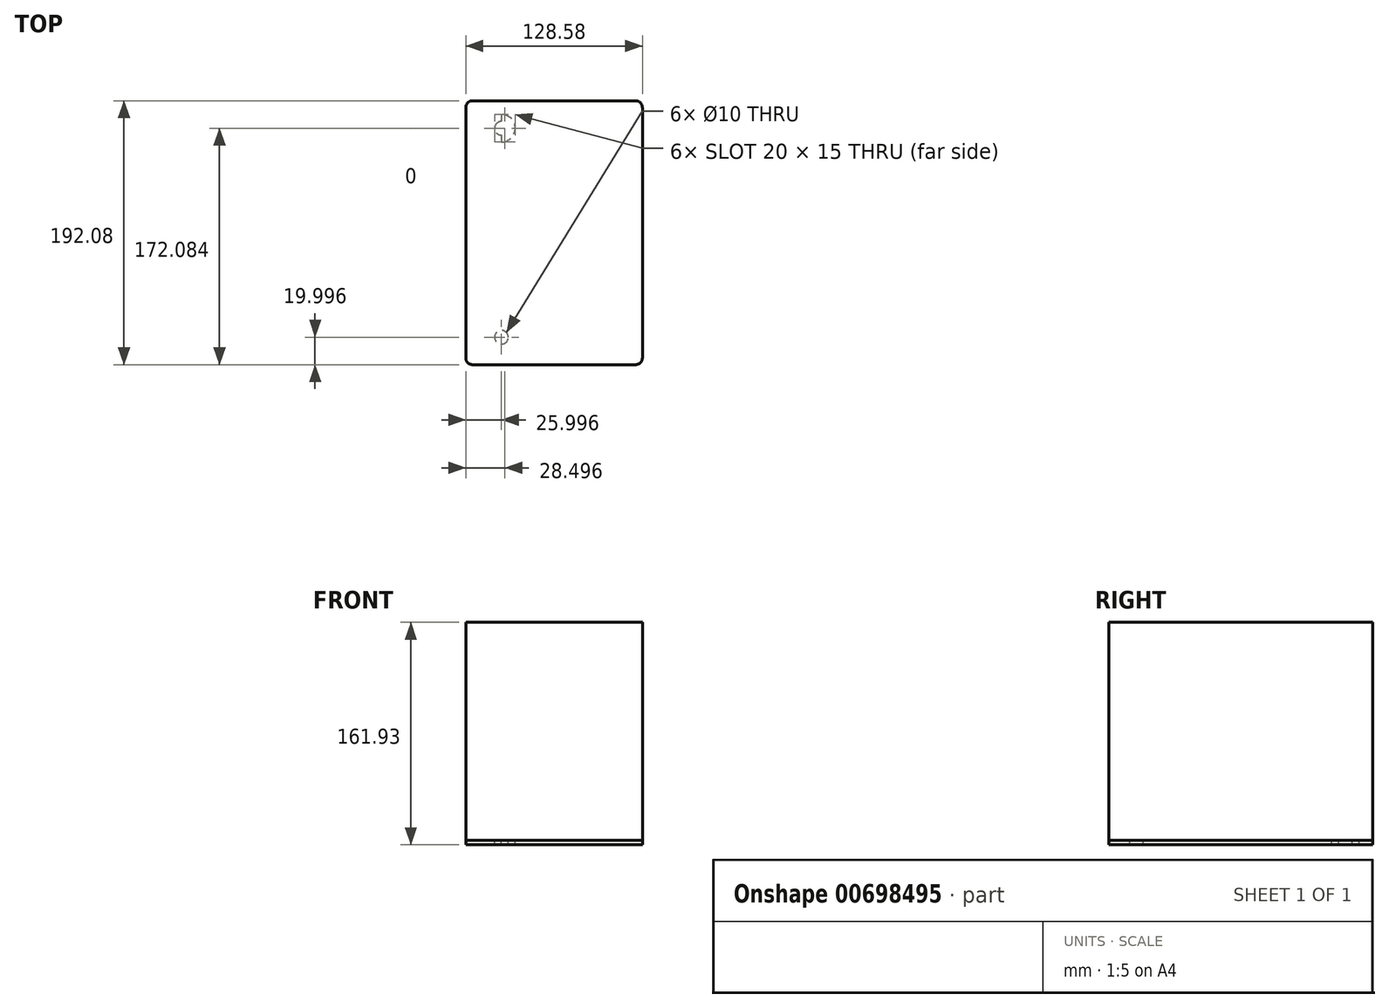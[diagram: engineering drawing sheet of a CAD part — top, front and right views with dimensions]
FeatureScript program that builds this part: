
annotation { "Feature Type Name" : "Feature", "Feature Type Description" : "" }
export const myFeature = defineFeature(function(context is Context, id is Id, definition is map)
    precondition{}
    {
        {
            var Q0;
            Q0=qCreatedBy(makeId("Top.planeOp"),FACE);
            var sketch = newSketch(context, id + "F0", { "sketchPlane" : qUnion([Q0])});
            skLineSegment(sketch, "E0.bottom", {"start": v(-59.3, -96.04) * mm, "end": v(59.3, -96.04) * mm});
            skLineSegment(sketch, "E0.top", {"start": v(-59.3, 96.04) * mm, "end": v(59.3, 96.04) * mm});
            skLineSegment(sketch, "E0.left", {"start": v(-64.3, -91.04) * mm, "end": v(-64.3, 91.04) * mm});
            skLineSegment(sketch, "E0.right", {"start": v(64.3, -91.04) * mm, "end": v(64.3, 91.04) * mm});
            skPoint(sketch, "E1.visualSharp", {"position": v(-64.3, -96.04) * mm});
            skArc(sketch, "E1.filletArc", {"start": v(-64.3, -91.04) * mm, "mid": v(-62.83, -94.58) * mm, "end": v(-59.3, -96.04) * mm});
            skPoint(sketch, "E2.visualSharp", {"position": v(-64.3, 96.04) * mm});
            skArc(sketch, "E2.filletArc", {"start": v(-59.3, 96.04) * mm, "mid": v(-62.83, 94.58) * mm, "end": v(-64.3, 91.04) * mm});
            skPoint(sketch, "E3.visualSharp", {"position": v(64.3, 96.04) * mm});
            skArc(sketch, "E3.filletArc", {"start": v(64.3, 91.04) * mm, "mid": v(62.83, 94.58) * mm, "end": v(59.3, 96.04) * mm});
            skPoint(sketch, "E4.visualSharp", {"position": v(64.3, -96.04) * mm});
            skArc(sketch, "E4.filletArc", {"start": v(59.3, -96.04) * mm, "mid": v(62.83, -94.58) * mm, "end": v(64.3, -91.04) * mm});
            skSolve(sketch);
        }
        {
            var Q0;
            Q0 = qSketchRegion(id + "F0", true);
            extrude(context, id + "F1", {"entities" : qUnion([Q0]), "depth" : 158.75 * mm, "offsetDistance" : 25 * mm});
        }
        {
            var Q0;
            Q0=makeQuery(id+"F1.opExtrude","CAP_FACE",FACE,{"disambiguationData":[OSD([sQuery(id+"F0.wireOp",EDGE,"E0.bottom"),sQuery(id+"F0.wireOp",EDGE,"E0.top"),sQuery(id+"F0.wireOp",EDGE,"E0.left"),sQuery(id+"F0.wireOp",EDGE,"E0.right"),sQuery(id+"F0.wireOp",EDGE,"E1.filletArc"),sQuery(id+"F0.wireOp",EDGE,"E2.filletArc"),sQuery(id+"F0.wireOp",EDGE,"E3.filletArc"),sQuery(id+"F0.wireOp",EDGE,"E4.filletArc")])],"isStart":true});
            var sketch = newSketch(context, id + "F2", { "sketchPlane" : qUnion([Q0])});
            skLineSegment(sketch, "E5.bottom", {"start": v(-38.3, 86.04) * mm, "end": v(-58.3, 86.04) * mm});
            skLineSegment(sketch, "E5.top", {"start": v(-38.3, 66.04) * mm, "end": v(-58.3, 66.04) * mm});
            skLineSegment(sketch, "E5.left", {"start": v(-38.3, 86.04) * mm, "end": v(-38.3, 66.04) * mm});
            skLineSegment(sketch, "E5.right", {"start": v(-58.3, 86.04) * mm, "end": v(-58.3, 66.04) * mm});
            skArc(sketch, "E6", {"start": v(-38.3, 66.04) * mm, "mid": v(-28.3, 76.04) * mm, "end": v(-38.3, 86.04) * mm});
            skCircle(sketch, "E7", {"center": v(-38.3, 76.04) * mm, "radius": 5 * mm});
            skLineSegment(sketch, "E8", {"start": v(-53.01, 0) * mm, "end": v(36.14, 0) * mm, "construction": true});
            skLineSegment(sketch, "E9.MirrorCS", {"start": v(-38.3, -86.04) * mm, "end": v(-58.3, -86.04) * mm});
            skCircle(sketch, "E10.MirrorC", {"center": v(-38.3, -76.04) * mm, "radius": 5 * mm});
            skLineSegment(sketch, "E11.MirrorCS", {"start": v(-38.3, -86.04) * mm, "end": v(-38.3, -66.04) * mm});
            skLineSegment(sketch, "E12.MirrorCS", {"start": v(-38.3, -66.04) * mm, "end": v(-58.3, -66.04) * mm});
            skArc(sketch, "E13.MirrorCS", {"start": v(-38.3, -66.04) * mm, "mid": v(-28.3, -76.04) * mm, "end": v(-38.3, -86.04) * mm});
            skLineSegment(sketch, "E14.MirrorCS", {"start": v(-58.3, -86.04) * mm, "end": v(-58.3, -66.04) * mm});
            skSolve(sketch);
        }
        {
            var Q0;
            {var subQ5=sQuery(id+"F2.wireOp",EDGE,"E5.bottom");Q0=makeQuery(id+"F2.imprint","IMPRINT",FACE,{"disambiguationData":[TD([[makeQuery(id+"F2.imprint","IMPRINT",EDGE,{"derivedFrom":subQ5}),1.0]])]});}
            var Q1;
            {var subQ0=sQuery(id+"F2.wireOp",EDGE,"E6");Q1=makeQuery(id+"F2.imprint","IMPRINT",FACE,{"disambiguationData":[TD([[makeQuery(id+"F2.imprint","IMPRINT",EDGE,{"derivedFrom":subQ0}),1.0]])]});}
            var Q2;
            {var subQ2=sQuery(id+"F2.wireOp",EDGE,"E9.MirrorCS");Q2=makeQuery(id+"F2.imprint","IMPRINT",FACE,{"disambiguationData":[TD([[makeQuery(id+"F2.imprint","IMPRINT",EDGE,{"derivedFrom":subQ2}),-1.0]])]});}
            var Q3;
            {var subQ4=sQuery(id+"F2.wireOp",EDGE,"E13.MirrorCS");Q3=makeQuery(id+"F2.imprint","IMPRINT",FACE,{"disambiguationData":[TD([[makeQuery(id+"F2.imprint","IMPRINT",EDGE,{"derivedFrom":subQ4}),-1.0]])]});}
            extrude(context, id + "F3", {"entities" : qUnion([Q0, Q1, Q2, Q3]), "depth" : 3.17 * mm, "offsetDistance" : 25 * mm});
        }
    });
